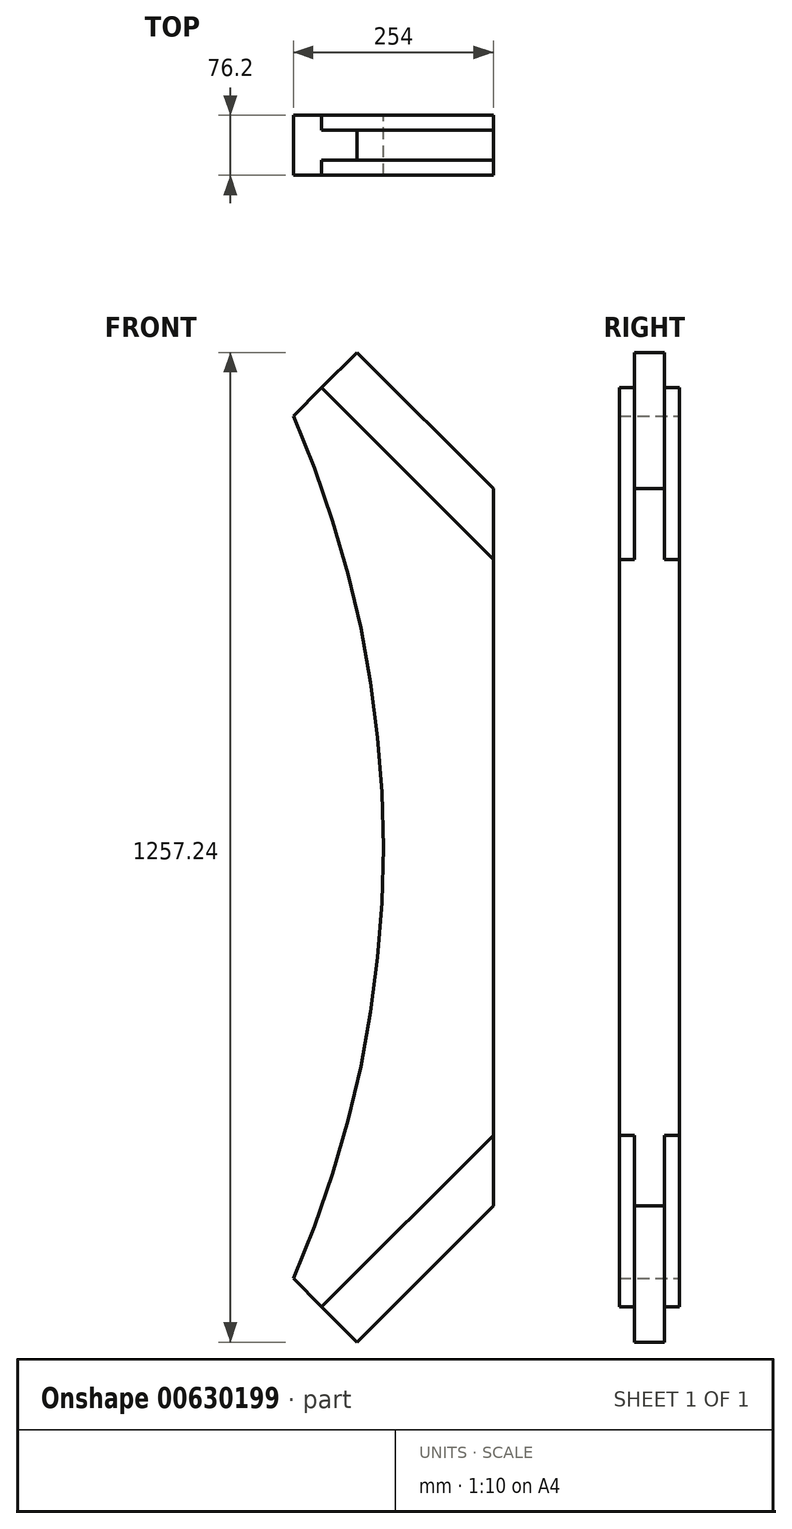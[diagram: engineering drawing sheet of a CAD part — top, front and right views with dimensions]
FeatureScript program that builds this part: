
annotation { "Feature Type Name" : "Feature", "Feature Type Description" : "" }
export const myFeature = defineFeature(function(context is Context, id is Id, definition is map)
    precondition{}
    {
        {
            var Q0;
            Q0=qCreatedBy(makeId("Front.planeOp"),FACE);
            var sketch = newSketch(context, id + "F0", { "sketchPlane" : qUnion([Q0])});
            skLineSegment(sketch, "E0.bottom", {"start": v(-127, 698.5) * mm, "end": v(127, 698.5) * mm});
            skLineSegment(sketch, "E0.top", {"start": v(-127, -698.5) * mm, "end": v(127, -698.5) * mm});
            skLineSegment(sketch, "E0.left", {"start": v(-127, 698.5) * mm, "end": v(-127, -698.5) * mm});
            skLineSegment(sketch, "E0.right", {"start": v(127, 698.5) * mm, "end": v(127, -698.5) * mm});
            skPoint(sketch, "E0.middle", {"position": v(0, 0) * mm});
            skLineSegment(sketch, "E1", {"start": v(-127, 543.35) * mm, "end": v(127, 289.35) * mm});
            skLineSegment(sketch, "E2", {"start": v(-127, 543.35) * mm, "end": v(-46.18, 624.17) * mm});
            skLineSegment(sketch, "E3", {"start": v(-46.18, 624.17) * mm, "end": v(127, 451) * mm});
            skLineSegment(sketch, "E4", {"start": v(-91.08, 579.27) * mm, "end": v(127, 361.2) * mm});
            skLineSegment(sketch, "E5", {"start": v(127, -298.24) * mm, "end": v(-127, -552.24) * mm});
            skLineSegment(sketch, "E6", {"start": v(-127, -552.24) * mm, "end": v(-46.18, -633.07) * mm});
            skLineSegment(sketch, "E7", {"start": v(-46.18, -633.07) * mm, "end": v(127, -459.89) * mm});
            skLineSegment(sketch, "E8", {"start": v(127, -370.09) * mm, "end": v(-91.08, -588.17) * mm});
            skArc(sketch, "E9", {"start": v(-127, -552.24) * mm, "mid": v(-12.7, -4.45) * mm, "end": v(-127, 543.35) * mm});
            skLineSegment(sketch, "E10", {"start": v(-100.06, -579.19) * mm, "end": v(127, -352.13) * mm});
            skLineSegment(sketch, "E11", {"start": v(-100.06, 570.3) * mm, "end": v(127, 343.23) * mm});
            skSolve(sketch);
        }
        {
            var Q0;
            {var subQ0=sQuery(id+"F0.wireOp",EDGE,"E1");Q0=makeQuery(id+"F0.imprint","IMPRINT",FACE,{"disambiguationData":[TD([[makeQuery(id+"F0.imprint","IMPRINT",EDGE,{"derivedFrom":subQ0}),-1.0]])]});}
            var Q1;
            {var subQ0=sQuery(id+"F0.wireOp",EDGE,"E5");Q1=makeQuery(id+"F0.imprint","IMPRINT",FACE,{"disambiguationData":[TD([[makeQuery(id+"F0.imprint","IMPRINT",EDGE,{"derivedFrom":subQ0}),1.0]])]});}
            var Q2;
            {var subQ0=sQuery(id+"F0.wireOp",EDGE,"E1");Q2=makeQuery(id+"F0.imprint","IMPRINT",FACE,{"disambiguationData":[TD([[makeQuery(id+"F0.imprint","IMPRINT",EDGE,{"derivedFrom":subQ0}),1.0]])]});}
            var Q3;
            {var subQ0=sQuery(id+"F0.wireOp",EDGE,"E4");Q3=makeQuery(id+"F0.imprint","IMPRINT",FACE,{"disambiguationData":[TD([[makeQuery(id+"F0.imprint","IMPRINT",EDGE,{"derivedFrom":subQ0}),-1.0]])]});}
            var Q4;
            {var subQ0=sQuery(id+"F0.wireOp",EDGE,"E8");Q4=makeQuery(id+"F0.imprint","IMPRINT",FACE,{"disambiguationData":[TD([[makeQuery(id+"F0.imprint","IMPRINT",EDGE,{"derivedFrom":subQ0}),-1.0]])]});}
            extrude(context, id + "F1", {"entities" : qUnion([Q0, Q1, Q2, Q3, Q4]), "endBound" : BoundingType.SYMMETRIC, "depth" : 76.2 * mm, "offsetDistance" : 25.4 * mm});
        }
        {
            var Q0;
            {var subQ0=sQuery(id+"F0.wireOp",EDGE,"E3");Q0=makeQuery(id+"F0.imprint","IMPRINT",FACE,{"disambiguationData":[TD([[makeQuery(id+"F0.imprint","IMPRINT",EDGE,{"derivedFrom":subQ0}),-1.0]])]});}
            var Q1;
            {var subQ0=sQuery(id+"F0.wireOp",EDGE,"E7");Q1=makeQuery(id+"F0.imprint","IMPRINT",FACE,{"disambiguationData":[TD([[makeQuery(id+"F0.imprint","IMPRINT",EDGE,{"derivedFrom":subQ0}),1.0]])]});}
            extrude(context, id + "F2", {"entities" : qUnion([Q0, Q1]), "operationType" : NewBodyOperationType.ADD, "endBound" : BoundingType.SYMMETRIC, "depth" : 38.1 * mm, "offsetDistance" : 25.4 * mm});
        }
    });
